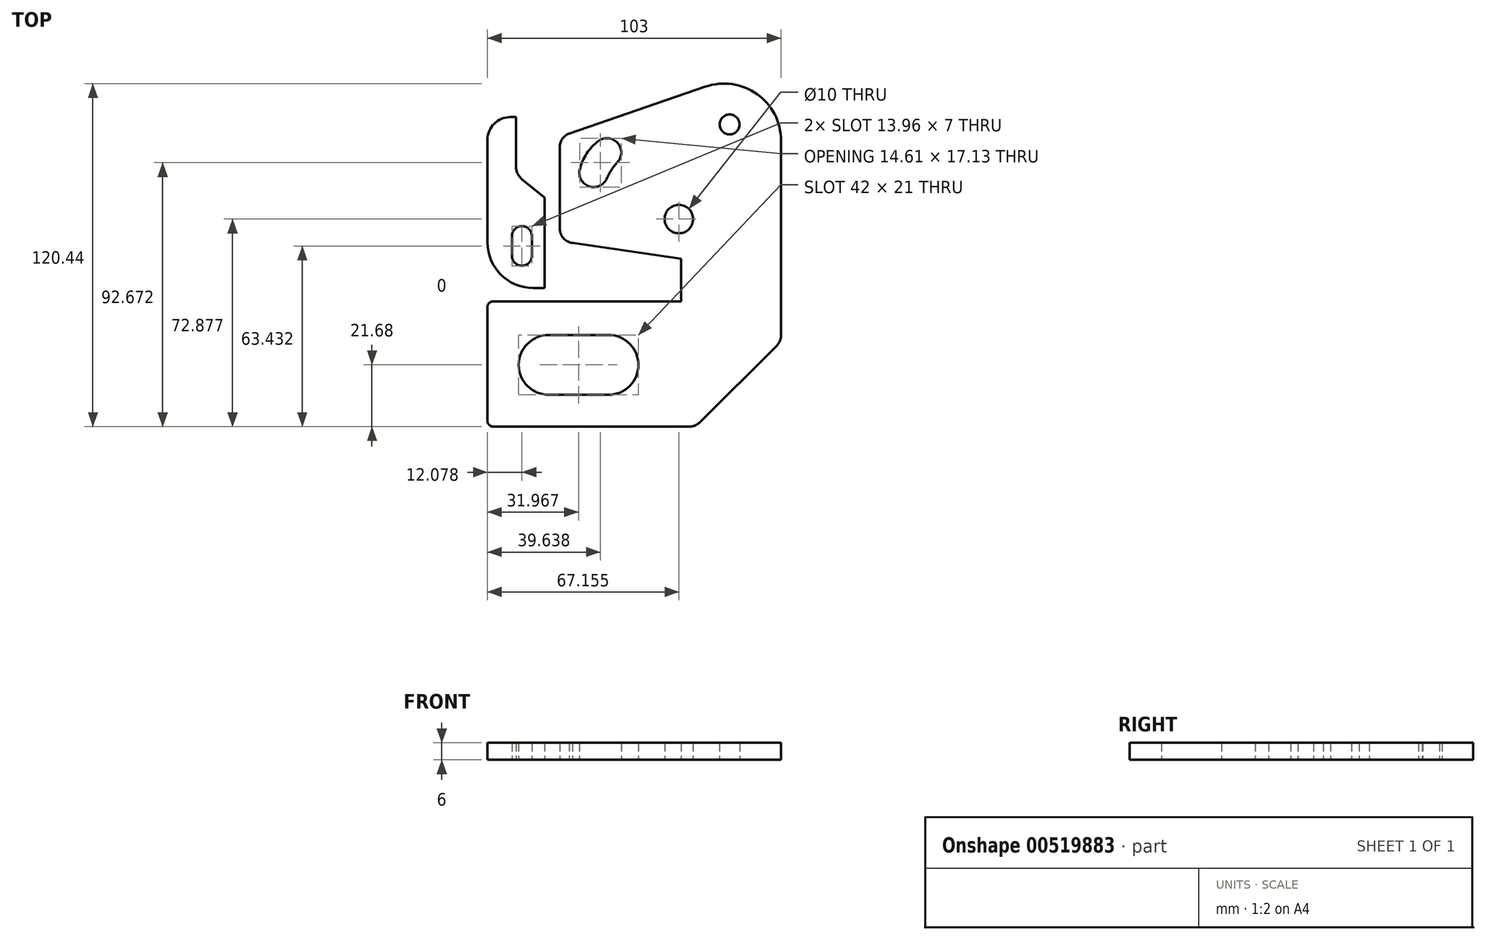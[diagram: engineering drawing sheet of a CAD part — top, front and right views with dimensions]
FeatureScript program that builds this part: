
annotation { "Feature Type Name" : "Feature", "Feature Type Description" : "" }
export const myFeature = defineFeature(function(context is Context, id is Id, definition is map)
    precondition{}
    {
        {
            var Q0;
            Q0=qCreatedBy(makeId("Top.planeOp"),FACE);
            var sketch = newSketch(context, id + "F0", { "sketchPlane" : qUnion([Q0])});
            skLineSegment(sketch, "E0.bottom", {"start": v(-49.8, -4.68) * mm, "end": v(16.16, -4.68) * mm});
            skLineSegment(sketch, "E0.top", {"start": v(-49.8, -48.68) * mm, "end": v(19.12, -48.68) * mm});
            skLineSegment(sketch, "E0.left", {"start": v(-51.8, -6.68) * mm, "end": v(-51.8, -46.68) * mm});
            skLineSegment(sketch, "E0.right", {"start": v(51.2, -4.68) * mm, "end": v(51.2, -16.65) * mm});
            skArc(sketch, "E1", {"start": v(-30.33, -16.5) * mm, "mid": v(-40.83, -27) * mm, "end": v(-30.33, -37.5) * mm});
            skArc(sketch, "E2", {"start": v(-9.33, -37.5) * mm, "mid": v(1.17, -27) * mm, "end": v(-9.33, -16.5) * mm});
            skLineSegment(sketch, "E3", {"start": v(-30.33, -16.5) * mm, "end": v(-9.33, -16.5) * mm});
            skLineSegment(sketch, "E4", {"start": v(-30.33, -37.5) * mm, "end": v(-9.33, -37.5) * mm});
            skLineSegment(sketch, "E5", {"start": v(16.16, -4.68) * mm, "end": v(16.16, 10.32) * mm});
            skLineSegment(sketch, "E6", {"start": v(49.73, -20.18) * mm, "end": v(22.66, -47.22) * mm});
            skLineSegment(sketch, "E7", {"start": v(-26.42, 49.51) * mm, "end": v(-26.42, 20.8) * mm});
            skArc(sketch, "E8.filletArc", {"start": v(-26.42, 20.8) * mm, "mid": v(-25.15, 17.47) * mm, "end": v(-21.98, 15.83) * mm});
            skArc(sketch, "E9.filletArc", {"start": v(49.73, -20.18) * mm, "mid": v(50.82, -18.56) * mm, "end": v(51.2, -16.65) * mm});
            skLineSegment(sketch, "E10", {"start": v(24.67, 70.67) * mm, "end": v(-23.12, 54.2) * mm});
            skArc(sketch, "E11.filletArc", {"start": v(-23.12, 54.2) * mm, "mid": v(-25.51, 52.38) * mm, "end": v(-26.42, 49.51) * mm});
            skArc(sketch, "E12.filletArc", {"start": v(19.12, -48.68) * mm, "mid": v(21.04, -48.3) * mm, "end": v(22.66, -47.22) * mm});
            skCircle(sketch, "E13", {"center": v(15.35, 24.2) * mm, "radius": 5 * mm});
            skArc(sketch, "E14", {"start": v(-19.41, 41.48) * mm, "mid": v(-16.07, 35.66) * mm, "end": v(-9.95, 38.41) * mm});
            skArc(sketch, "E15", {"start": v(-6.17, 44.2) * mm, "mid": v(-6.13, 50.92) * mm, "end": v(-12.8, 51.63) * mm});
            skArc(sketch, "E16", {"start": v(-12.8, 51.63) * mm, "mid": v(-17.04, 47.16) * mm, "end": v(-19.41, 41.48) * mm});
            skArc(sketch, "E17", {"start": v(-6.17, 44.2) * mm, "mid": v(-8.3, 41.47) * mm, "end": v(-9.95, 38.41) * mm});
            skCircle(sketch, "E18", {"center": v(33.15, 57.4) * mm, "radius": 3.5 * mm});
            skLineSegment(sketch, "E19", {"start": v(51.19, 51.76) * mm, "end": v(51.2, 10.32) * mm});
            skLineSegment(sketch, "E20", {"start": v(51.2, -4.68) * mm, "end": v(51.2, 10.32) * mm});
            skArc(sketch, "E21.filletArc", {"start": v(-49.8, -4.68) * mm, "mid": v(-51.21, -5.27) * mm, "end": v(-51.8, -6.68) * mm});
            skArc(sketch, "E22.filletArc", {"start": v(-51.8, -46.68) * mm, "mid": v(-51.21, -48.1) * mm, "end": v(-49.8, -48.68) * mm});
            skLineSegment(sketch, "E23.trimOffspring", {"start": v(-21.98, 15.83) * mm, "end": v(16.16, 10.32) * mm});
            skArc(sketch, "E24", {"start": v(51.19, 51.76) * mm, "mid": v(42.8, 68.04) * mm, "end": v(24.67, 70.67) * mm});
            skLineSegment(sketch, "E25.trimOffspring", {"start": v(-31.8, 31.77) * mm, "end": v(-31.8, 0) * mm});
            skArc(sketch, "E26", {"start": v(-41.8, 42.77) * mm, "mid": v(-41.22, 40.2) * mm, "end": v(-39.59, 38.11) * mm});
            skLineSegment(sketch, "E27", {"start": v(-31.8, 31.77) * mm, "end": v(-39.59, 38.11) * mm});
            skLineSegment(sketch, "E28", {"start": v(-41.8, 60) * mm, "end": v(-41.8, 42.77) * mm});
            skLineSegment(sketch, "E29", {"start": v(-41.8, 60) * mm, "end": v(-43.8, 60) * mm});
            skLineSegment(sketch, "E30", {"start": v(-51.8, 52) * mm, "end": v(-51.8, 16) * mm});
            skArc(sketch, "E31.filletArc", {"start": v(-43.8, 60) * mm, "mid": v(-49.46, 57.66) * mm, "end": v(-51.8, 52) * mm});
            skArc(sketch, "E32.filletArc", {"start": v(-51.8, 16) * mm, "mid": v(-47.11, 4.69) * mm, "end": v(-35.8, 0) * mm});
            skLineSegment(sketch, "E33", {"start": v(-35.8, 0) * mm, "end": v(-31.8, 0) * mm});
            skArc(sketch, "E34", {"start": v(-36.22, 18.23) * mm, "mid": v(-39.72, 21.73) * mm, "end": v(-43.22, 18.23) * mm});
            skArc(sketch, "E35", {"start": v(-43.22, 11.27) * mm, "mid": v(-39.72, 7.77) * mm, "end": v(-36.22, 11.27) * mm});
            skLineSegment(sketch, "E36", {"start": v(-36.22, 18.23) * mm, "end": v(-36.22, 11.27) * mm});
            skLineSegment(sketch, "E37", {"start": v(-43.22, 18.23) * mm, "end": v(-43.22, 11.27) * mm});
            skSolve(sketch);
        }
        {
            var Q0;
            Q0=makeQuery(id+"F0.imprint","IMPRINT",FACE,{"disambiguationData":[TD([[makeQuery(id+"F0.imprint","IMPRINT",EDGE,{"derivedFrom":sQuery(id+"F0.wireOp",EDGE,"8W7yfe0H-aZix-Sv96-F4wC-eh7qvSx2GVEx")}),1.0]])]});
            var Q1;
            {var subQ3=sQuery(id+"F0.wireOp",EDGE,"E5");Q1=makeQuery(id+"F0.imprint","IMPRINT",FACE,{"disambiguationData":[TD([[makeQuery(id+"F0.imprint","IMPRINT",EDGE,{"derivedFrom":subQ3}),-1.0]])]});}
            var Q2;
            {var subQ1=sQuery(id+"F0.wireOp",EDGE,"E0.left");Q2=makeQuery(id+"F0.imprint","IMPRINT",FACE,{"disambiguationData":[TD([[makeQuery(id+"F0.imprint","IMPRINT",EDGE,{"derivedFrom":subQ1}),1.0]])]});}
            var Q3;
            Q3=makeQuery(id+"F0.imprint","IMPRINT",FACE,{"disambiguationData":[TD([[makeQuery(id+"F0.imprint","IMPRINT",EDGE,{"derivedFrom":sQuery(id+"F0.wireOp",EDGE,"E25.trimOffspring")}),-1.0]])]});
            extrude(context, id + "F1", {"entities" : qUnion([Q0, Q1, Q2, Q3]), "depth" : 6 * mm, "offsetDistance" : 25 * mm});
        }
        {
            var Q0;
            Q0=makeQuery(id+"F1.opExtrude","SWEPT_BODY",BODY,{"disambiguationData":[OSD([sQuery(id+"F0.wireOp",EDGE,"E25.trimOffspring"),sQuery(id+"F0.wireOp",EDGE,"E26"),sQuery(id+"F0.wireOp",EDGE,"E27"),sQuery(id+"F0.wireOp",EDGE,"E28"),sQuery(id+"F0.wireOp",EDGE,"E29"),sQuery(id+"F0.wireOp",EDGE,"E30"),sQuery(id+"F0.wireOp",EDGE,"E31.filletArc"),sQuery(id+"F0.wireOp",EDGE,"E32.filletArc"),sQuery(id+"F0.wireOp",EDGE,"E33"),sQuery(id+"F0.wireOp",EDGE,"E34"),sQuery(id+"F0.wireOp",EDGE,"E35"),sQuery(id+"F0.wireOp",EDGE,"E36"),sQuery(id+"F0.wireOp",EDGE,"E37")])]});
            transform(context, id + "F2", {"entities" : qUnion([Q0]), "transformType" : TransformType.TRANSLATION_3D, "dx" : 0 * mm, "dy" : 0 * mm, "dz" : 0 * mm, "makeCopy" : true});
        }
    });
